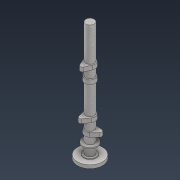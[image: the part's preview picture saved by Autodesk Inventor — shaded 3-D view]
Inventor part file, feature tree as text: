
AUTODESK INVENTOR PART (.ipt)
format: ipt  version: 2022 (Build 260153000, 153)  size: 217,600 bytes
history: native  units: mm
features: extrude x9, sketch x8, plane x7, fillet x2, hole x1
ambient origin geometry x8: Origin, YZ Plane, XZ Plane, XY Plane, X Axis, Y Axis, Z Axis, Center Point
bodies: Solid1 (feature_tree)
feature tree (27):
  extrude  "Extrusion1"  Depth=20.0mm
  plane  "Work Plane1"
  plane  "Work Plane2"
  plane  "Work Plane3"
  sketch  "Sketch2"  dims[d3=-101.515mm d4=15.0mm d5=-15.0mm d6=25.0mm]
  extrude  "Extrusion2"  Depth=15.0mm
  extrude  "Extrusion3"  Depth=10.0mm TaperAngle=0.0deg
  plane  "Work Plane4"
  plane  "Work Plane5"
  plane  "Work Plane6"
  fillet  "Fillet1"  Radius=25.0mm
  extrude  "Extrusion4"  Depth=10.0mm TaperAngle=0.0deg
  extrude  "Extrusion5"  Depth=15.0mm
  fillet  "Fillet2"  Radius=25.0mm
  sketch  "Sketch7"  dims[d22=1.745329mm d23=30.0mm]
  extrude  "Extrusion6"  Depth=30.0mm
  extrude  "Extrusion7"  Depth=10.0mm
  sketch  "Sketch8"  dims[d24=10.0mm d25=0.0mm d26=25.0mm]
  extrude  "Extrusion8"  Depth=30.0mm
  hole  "Hole1"  [1 undecoded]
  plane  "Work Plane7"
  extrude  "Extrusion9"  Depth=10.0mm TaperAngle=0.0deg
  sketch  "Sketch1"  dims[d0=283.0mm d1=0.0mm d2=20.0mm]
  sketch  "Sketch4"  dims[d7=30.0mm d8=10.0mm d9=0.0mm d10=25.0mm]
  sketch  "Sketch5"  dims[d12=30.0mm d13=10.0mm d14=0.0mm]
  sketch  "Sketch6"  dims[d15=5.0mm d16=-108.77mm d17=15.0mm d18=-15.0mm d19=43.633231mm d21=25.0mm]
  sketch  "Sketch9"  dims[d27=18.0mm d28=30.0mm d29=43.633231mm d30=10.0mm d31=0.0mm d32=5.0mm d33=30.0mm d34=60.0mm d35=8.0mm d36=0.0mm d37=10.0mm d38=0.0mm d39=30.0mm d41=360.0deg d43=45.0mm d44=5.0mm d45=30.0mm d46=5.0mm d47=0.0mm d48=10.0mm d49=4.134mm d50=5.0mm d51=4.0mm d52=2.0mm d53=90.0deg d54=5.0mm d55=0.0mm d56=21.76mm d57=35.0mm d58=3.0mm d59=0.0mm]
note: 1 required parameter value undecoded (feature->parameter linkage not recoverable at this tier; creation-order binding heuristic only, values carry confidence <= 0.55)
